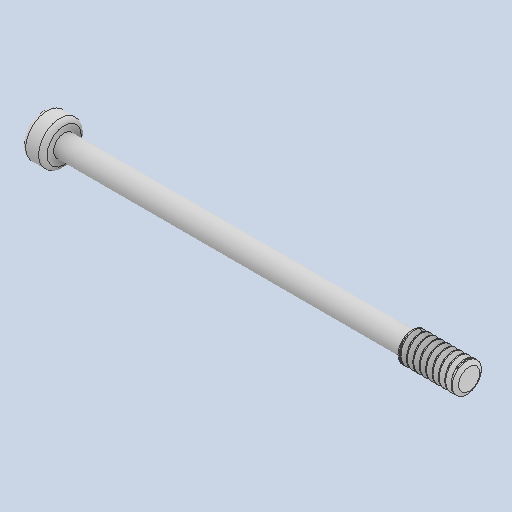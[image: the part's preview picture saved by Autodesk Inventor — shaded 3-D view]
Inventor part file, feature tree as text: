
AUTODESK INVENTOR PART (.ipt)
format: ipt  version: 2025.2 (Build 292293000, 293)  size: 235,520 bytes
history: native  units: mm
features: other x1, revolve x1
ambient origin geometry x8: Origin, YZ Plane, XZ Plane, XY Plane, X Axis, Y Axis, Z Axis, Center Point
bodies: Body1 (feature_tree)
feature tree (2):
  other  "Bryła1"
  revolve  "Revolve3"  [1 undecoded]
note: 1 required parameter value undecoded (feature->parameter linkage not recoverable at this tier; creation-order binding heuristic only, values carry confidence <= 0.55)
